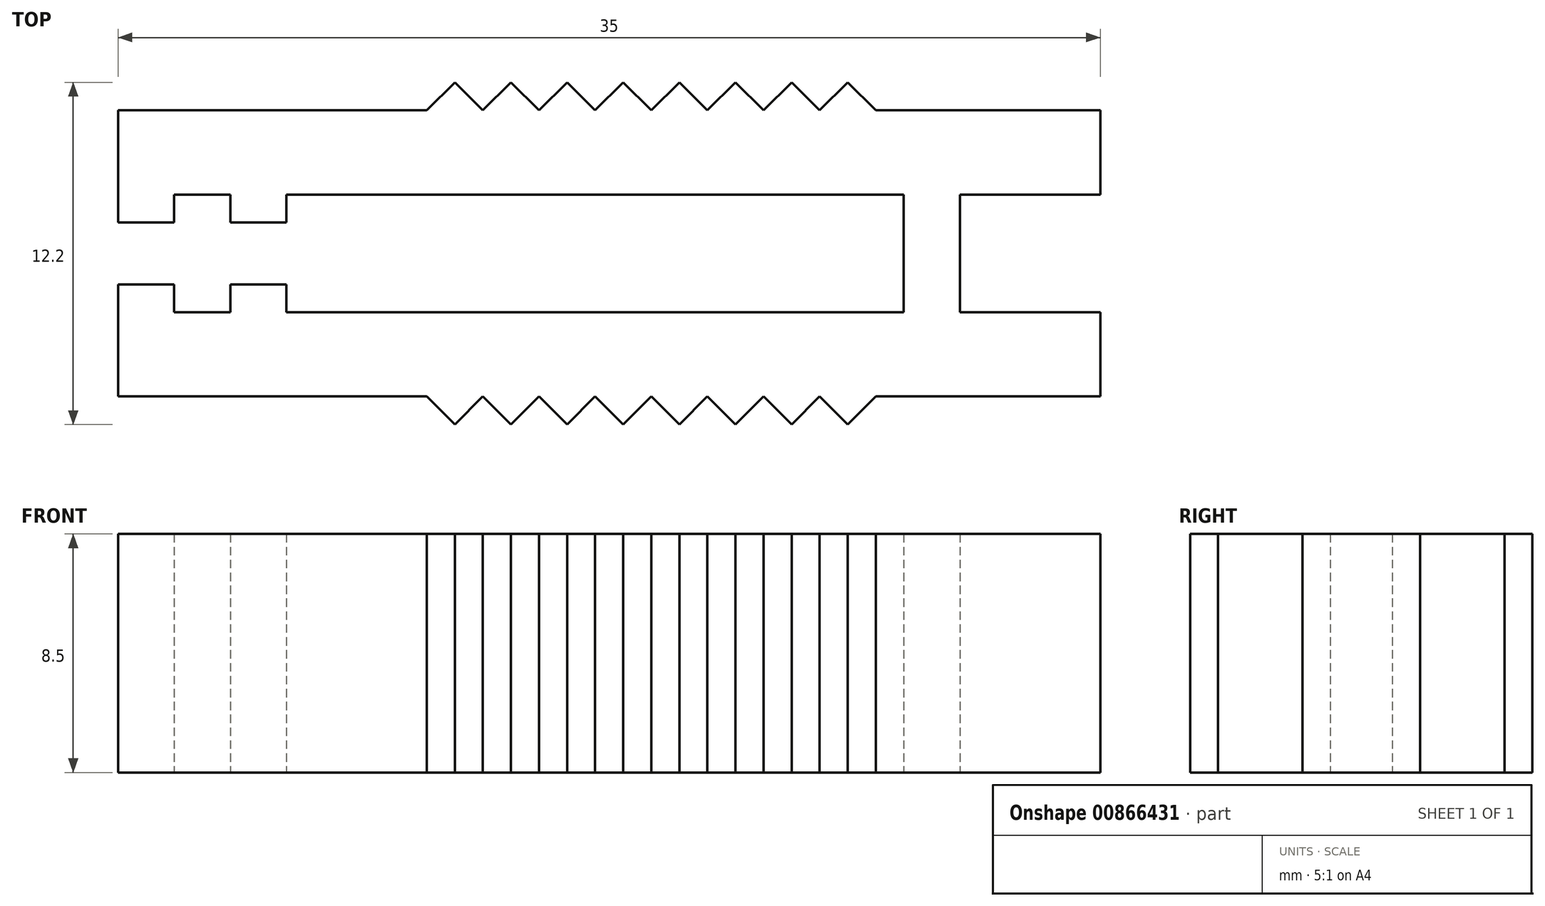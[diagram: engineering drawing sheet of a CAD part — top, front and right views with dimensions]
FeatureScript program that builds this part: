
annotation { "Feature Type Name" : "Feature", "Feature Type Description" : "" }
export const myFeature = defineFeature(function(context is Context, id is Id, definition is map)
    precondition{}
    {
        {
            var Q0;
            Q0=qCreatedBy(makeId("Top.planeOp"),FACE);
            var sketch = newSketch(context, id + "F0", { "sketchPlane" : qUnion([Q0])});
            skLineSegment(sketch, "E0", {"start": v(-113.65, 0) * mm, "end": v(109.65, 0) * mm, "construction": true});
            skPoint(sketch, "E1.oppositeSnap0", {"position": v(-2, 0) * mm});
            skLineSegment(sketch, "E1.bottom", {"start": v(-4, 0) * mm, "end": v(-2, 0) * mm});
            skLineSegment(sketch, "E1.left", {"start": v(-4, 0) * mm, "end": v(-4, 2.1) * mm});
            skLineSegment(sketch, "E1.right", {"start": v(-2, 0) * mm, "end": v(-2, 2.1) * mm});
            skLineSegment(sketch, "E2.bottom", {"start": v(-32, 5.1) * mm, "end": v(3, 5.1) * mm});
            skLineSegment(sketch, "E2.top", {"start": v(-30, 2.1) * mm, "end": v(-28, 2.1) * mm});
            skLineSegment(sketch, "E2.left", {"start": v(-32, 5.1) * mm, "end": v(-32, 2.1) * mm});
            skLineSegment(sketch, "E2.right", {"start": v(3, 5.1) * mm, "end": v(3, 2.1) * mm});
            skPoint(sketch, "E3", {"position": v(-2, 2.1) * mm});
            skLineSegment(sketch, "E4.top", {"start": v(-32, 1.1) * mm, "end": v(-30, 1.1) * mm});
            skLineSegment(sketch, "E4.left", {"start": v(-32, 2.1) * mm, "end": v(-32, 1.1) * mm});
            skLineSegment(sketch, "E4.right", {"start": v(-30, 2.1) * mm, "end": v(-30, 1.1) * mm});
            skPoint(sketch, "E5", {"position": v(-28, 2.1) * mm});
            skLineSegment(sketch, "E6.top", {"start": v(-28, 1.1) * mm, "end": v(-26, 1.1) * mm});
            skLineSegment(sketch, "E6.left", {"start": v(-28, 2.1) * mm, "end": v(-28, 1.1) * mm});
            skLineSegment(sketch, "E6.right", {"start": v(-26, 2.1) * mm, "end": v(-26, 1.1) * mm});
            skLineSegment(sketch, "E7.trimOffspring", {"start": v(-26, 2.1) * mm, "end": v(-4, 2.1) * mm});
            skLineSegment(sketch, "E8.trimOffspring", {"start": v(-2, 2.1) * mm, "end": v(3, 2.1) * mm});
            skLineSegment(sketch, "E9.MirrorCS", {"start": v(-30, -2.1) * mm, "end": v(-30, -1.1) * mm});
            skLineSegment(sketch, "E10.MirrorCS", {"start": v(-28, -2.1) * mm, "end": v(-28, -1.1) * mm});
            skLineSegment(sketch, "E11.MirrorCS", {"start": v(-26, -2.1) * mm, "end": v(-26, -1.1) * mm});
            skLineSegment(sketch, "E12.MirrorCS", {"start": v(-32, -2.1) * mm, "end": v(-32, -1.1) * mm});
            skLineSegment(sketch, "E13.MirrorCS", {"start": v(-32, -5.1) * mm, "end": v(3, -5.1) * mm});
            skLineSegment(sketch, "E14.MirrorCS", {"start": v(-28, -1.1) * mm, "end": v(-26, -1.1) * mm});
            skLineSegment(sketch, "E15.MirrorCS", {"start": v(-32, -5.1) * mm, "end": v(-32, -2.1) * mm});
            skLineSegment(sketch, "E16.MirrorCS", {"start": v(-32, -1.1) * mm, "end": v(-30, -1.1) * mm});
            skLineSegment(sketch, "E17.MirrorCS", {"start": v(3, -5.1) * mm, "end": v(3, -2.1) * mm});
            skPoint(sketch, "E18.MirrorP", {"position": v(-2, -2.1) * mm});
            skLineSegment(sketch, "E19.MirrorCS", {"start": v(-2, -2.1) * mm, "end": v(3, -2.1) * mm});
            skLineSegment(sketch, "E20.MirrorCS", {"start": v(-30, -2.1) * mm, "end": v(-28, -2.1) * mm});
            skLineSegment(sketch, "E21.MirrorCS", {"start": v(-26, -2.1) * mm, "end": v(-4, -2.1) * mm});
            skPoint(sketch, "E22.MirrorP", {"position": v(-28, -2.1) * mm});
            skLineSegment(sketch, "E23.MirrorCS", {"start": v(-4, 0) * mm, "end": v(-4, -2.1) * mm});
            skLineSegment(sketch, "E24.MirrorCS", {"start": v(-2, 0) * mm, "end": v(-2, -2.1) * mm});
            skPoint(sketch, "E25", {"position": v(-5, 5.1) * mm});
            skPoint(sketch, "E26", {"position": v(-7, 5.1) * mm});
            skPoint(sketch, "E27", {"position": v(-9, 5.1) * mm});
            skPoint(sketch, "E28", {"position": v(-11, 5.1) * mm});
            skPoint(sketch, "E29", {"position": v(-13, 5.1) * mm});
            skPoint(sketch, "E30", {"position": v(-15, 5.1) * mm});
            skPoint(sketch, "E31", {"position": v(-17, 5.1) * mm});
            skPoint(sketch, "E32", {"position": v(-6, 6.1) * mm});
            skPoint(sketch, "E33", {"position": v(-19, 5.1) * mm});
            skPoint(sketch, "E34", {"position": v(-21, 5.1) * mm});
            skPoint(sketch, "E35", {"position": v(-20, 6.1) * mm});
            skLineSegment(sketch, "E36", {"start": v(-22.91, 6.1) * mm, "end": v(-3.4, 6.1) * mm, "construction": true});
            skPoint(sketch, "E37", {"position": v(-8, 6.1) * mm});
            skPoint(sketch, "E38", {"position": v(-10, 6.1) * mm});
            skPoint(sketch, "E39", {"position": v(-12, 6.1) * mm});
            skPoint(sketch, "E40", {"position": v(-14, 6.1) * mm});
            skPoint(sketch, "E41", {"position": v(-18, 6.1) * mm});
            skPoint(sketch, "E42", {"position": v(-16, 6.1) * mm});
            skLineSegment(sketch, "E43", {"start": v(-5, 5.1) * mm, "end": v(-6, 6.1) * mm});
            skLineSegment(sketch, "E44", {"start": v(-6, 6.1) * mm, "end": v(-7, 5.1) * mm});
            skLineSegment(sketch, "E45", {"start": v(-7, 5.1) * mm, "end": v(-8, 6.1) * mm});
            skLineSegment(sketch, "E46", {"start": v(-8, 6.1) * mm, "end": v(-9, 5.1) * mm});
            skLineSegment(sketch, "E47", {"start": v(-9, 5.1) * mm, "end": v(-10, 6.1) * mm});
            skLineSegment(sketch, "E48", {"start": v(-10, 6.1) * mm, "end": v(-11, 5.1) * mm});
            skLineSegment(sketch, "E49", {"start": v(-12, 6.1) * mm, "end": v(-13, 5.1) * mm});
            skLineSegment(sketch, "E50", {"start": v(-13, 5.1) * mm, "end": v(-14, 6.1) * mm});
            skLineSegment(sketch, "E51", {"start": v(-14, 6.1) * mm, "end": v(-15, 5.1) * mm});
            skLineSegment(sketch, "E52", {"start": v(-15, 5.1) * mm, "end": v(-16, 6.1) * mm});
            skLineSegment(sketch, "E53", {"start": v(-16, 6.1) * mm, "end": v(-17, 5.1) * mm});
            skLineSegment(sketch, "E54", {"start": v(-17, 5.1) * mm, "end": v(-18, 6.1) * mm});
            skLineSegment(sketch, "E55", {"start": v(-18, 6.1) * mm, "end": v(-19, 5.1) * mm});
            skLineSegment(sketch, "E56", {"start": v(-19, 5.1) * mm, "end": v(-20, 6.1) * mm});
            skLineSegment(sketch, "E57", {"start": v(-20, 6.1) * mm, "end": v(-21, 5.1) * mm});
            skLineSegment(sketch, "E58", {"start": v(-11, 5.1) * mm, "end": v(-12, 6.1) * mm});
            skPoint(sketch, "E59.MirrorP", {"position": v(-17, -5.1) * mm});
            skLineSegment(sketch, "E60.MirrorCS", {"start": v(-15, -5.1) * mm, "end": v(-16, -6.1) * mm});
            skPoint(sketch, "E61.MirrorP", {"position": v(-12, -6.1) * mm});
            skPoint(sketch, "E62.MirrorP", {"position": v(-15, -5.1) * mm});
            skPoint(sketch, "E63.MirrorP", {"position": v(-11, -5.1) * mm});
            skLineSegment(sketch, "E64.MirrorCS", {"start": v(-13, -5.1) * mm, "end": v(-14, -6.1) * mm});
            skLineSegment(sketch, "E65.MirrorCS", {"start": v(-10, -6.1) * mm, "end": v(-11, -5.1) * mm});
            skPoint(sketch, "E66.MirrorP", {"position": v(-13, -5.1) * mm});
            skLineSegment(sketch, "E67.MirrorCS", {"start": v(-5, -5.1) * mm, "end": v(-6, -6.1) * mm});
            skPoint(sketch, "E68.MirrorP", {"position": v(-20, -6.1) * mm});
            skLineSegment(sketch, "E69.MirrorCS", {"start": v(-6, -6.1) * mm, "end": v(-7, -5.1) * mm});
            skLineSegment(sketch, "E70.MirrorCS", {"start": v(-11, -5.1) * mm, "end": v(-12, -6.1) * mm});
            skLineSegment(sketch, "E71.MirrorCS", {"start": v(-14, -6.1) * mm, "end": v(-15, -5.1) * mm});
            skPoint(sketch, "E72.MirrorP", {"position": v(-9, -5.1) * mm});
            skLineSegment(sketch, "E73.MirrorCS", {"start": v(-9, -5.1) * mm, "end": v(-10, -6.1) * mm});
            skPoint(sketch, "E74.MirrorP", {"position": v(-10, -6.1) * mm});
            skLineSegment(sketch, "E75.MirrorCS", {"start": v(-17, -5.1) * mm, "end": v(-18, -6.1) * mm});
            skLineSegment(sketch, "E76.MirrorCS", {"start": v(-12, -6.1) * mm, "end": v(-13, -5.1) * mm});
            skPoint(sketch, "E77.MirrorP", {"position": v(-19, -5.1) * mm});
            skLineSegment(sketch, "E78.MirrorCS", {"start": v(-20, -6.1) * mm, "end": v(-21, -5.1) * mm});
            skPoint(sketch, "E79.MirrorP", {"position": v(-14, -6.1) * mm});
            skLineSegment(sketch, "E80.MirrorCS", {"start": v(-18, -6.1) * mm, "end": v(-19, -5.1) * mm});
            skPoint(sketch, "E81.MirrorP", {"position": v(-6, -6.1) * mm});
            skLineSegment(sketch, "E82.MirrorCS", {"start": v(-8, -6.1) * mm, "end": v(-9, -5.1) * mm});
            skPoint(sketch, "E83.MirrorP", {"position": v(-5, -5.1) * mm});
            skLineSegment(sketch, "E84.MirrorCS", {"start": v(-19, -5.1) * mm, "end": v(-20, -6.1) * mm});
            skPoint(sketch, "E85.MirrorP", {"position": v(-18, -6.1) * mm});
            skPoint(sketch, "E86.MirrorP", {"position": v(-16, -6.1) * mm});
            skPoint(sketch, "E87.MirrorP", {"position": v(-21, -5.1) * mm});
            skPoint(sketch, "E88.MirrorP", {"position": v(-8, -6.1) * mm});
            skLineSegment(sketch, "E89.MirrorCS", {"start": v(-16, -6.1) * mm, "end": v(-17, -5.1) * mm});
            skLineSegment(sketch, "E90.MirrorCS", {"start": v(-22.91, -6.1) * mm, "end": v(-3.4, -6.1) * mm, "construction": true});
            skPoint(sketch, "E91.MirrorP", {"position": v(-7, -5.1) * mm});
            skLineSegment(sketch, "E92.MirrorCS", {"start": v(-7, -5.1) * mm, "end": v(-8, -6.1) * mm});
            skSolve(sketch);
        }
        {
            var Q0;
            Q0 = qSketchRegion(id + "F0", true);
            extrude(context, id + "F1", {"entities" : qUnion([Q0]), "depth" : 8.5 * mm, "offsetDistance" : 25 * mm});
        }
    });
